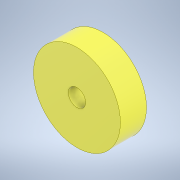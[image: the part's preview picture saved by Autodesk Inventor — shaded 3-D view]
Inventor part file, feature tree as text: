
AUTODESK INVENTOR PART (.ipt)
format: ipt  version: 2020 (Build 240168000, 168)  size: 97,792 bytes
history: native  units: mm
features: extrude x1, sketch x1
ambient origin geometry x8: Origin, YZ Plane, XZ Plane, XY Plane, X Axis, Y Axis, Z Axis, Center Point
bodies: Solid1 (feature_tree)
feature tree (2):
  extrude  "Extrusion1"  Depth=3.0mm
  sketch  "Sketch1"  dims[d0=10.0mm d1=2.0mm d2=3.0mm d3=0.0mm]
